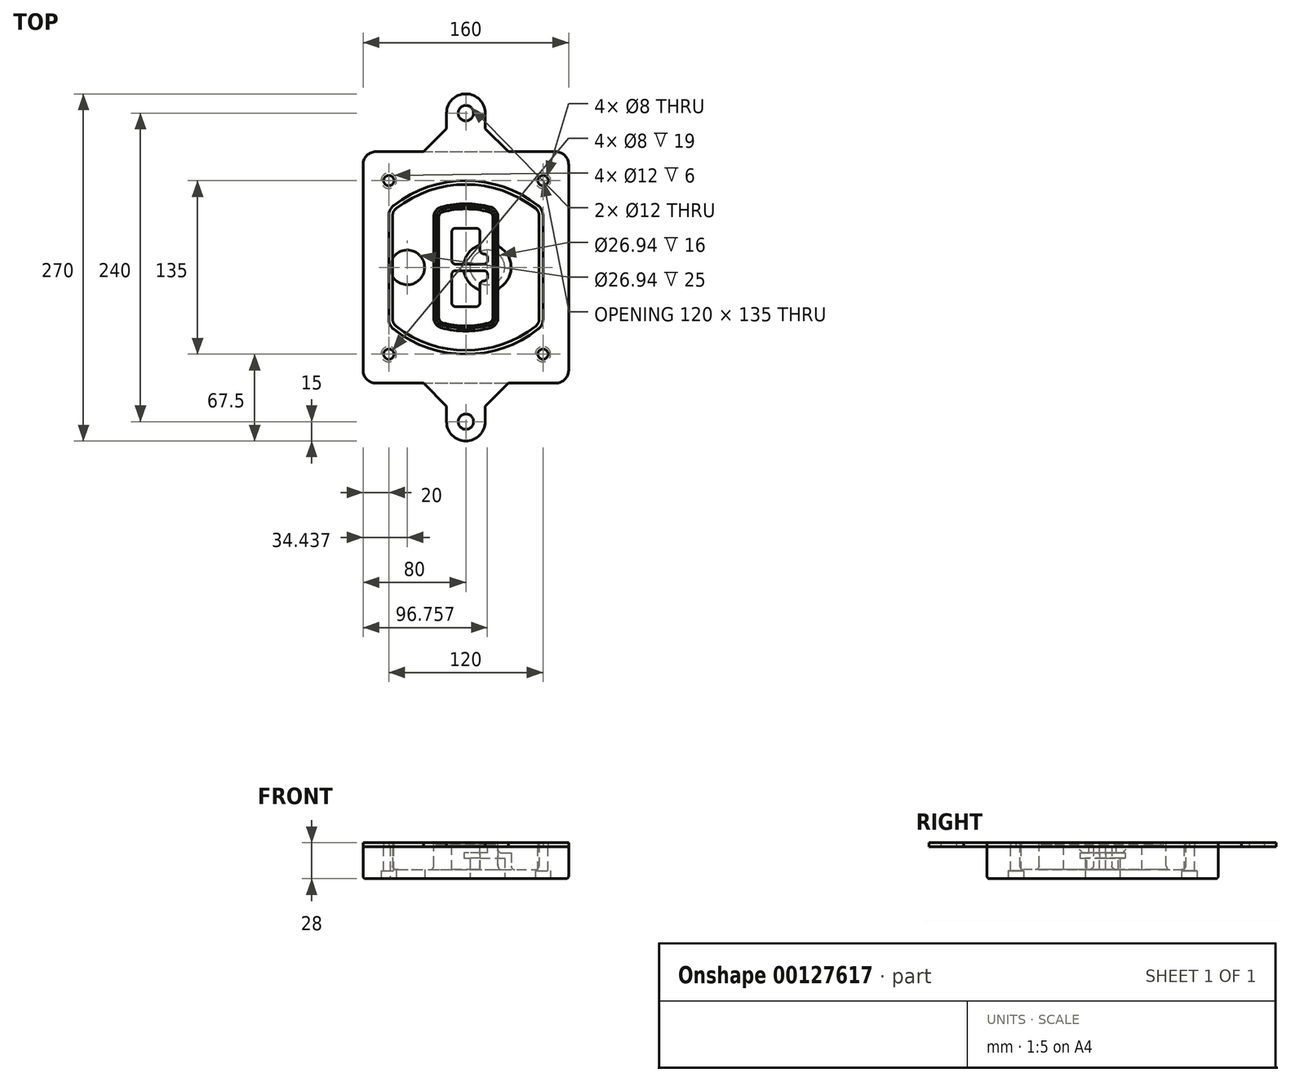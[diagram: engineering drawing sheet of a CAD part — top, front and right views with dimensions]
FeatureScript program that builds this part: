
annotation { "Feature Type Name" : "Feature", "Feature Type Description" : "" }
export const myFeature = defineFeature(function(context is Context, id is Id, definition is map)
    precondition{}
    {
        {
            var Q0;
            Q0=qCreatedBy(makeId("Top.planeOp"),FACE);
            var sketch = newSketch(context, id + "F0", { "sketchPlane" : qUnion([Q0])});
            skPoint(sketch, "E0.rect.middle", {"position": v(0, 0) * mm});
            skLineSegment(sketch, "E1.bottom", {"start": v(-70, -90) * mm, "end": v(70, -90) * mm});
            skLineSegment(sketch, "E1.top", {"start": v(-70, 90) * mm, "end": v(70, 90) * mm});
            skLineSegment(sketch, "E1.left", {"start": v(-80, -80) * mm, "end": v(-80, 80) * mm});
            skLineSegment(sketch, "E1.right", {"start": v(80, -80) * mm, "end": v(80, 80) * mm});
            skLineSegment(sketch, "E2", {"start": v(-80, 90) * mm, "end": v(80, -90) * mm, "construction": true});
            skLineSegment(sketch, "E3", {"start": v(80, 90) * mm, "end": v(-80, -90) * mm, "construction": true});
            skCircle(sketch, "E4", {"center": v(-60, 67.5) * mm, "radius": 4 * mm});
            skCircle(sketch, "E5", {"center": v(60, 67.5) * mm, "radius": 4 * mm});
            skCircle(sketch, "E6", {"center": v(60, -67.5) * mm, "radius": 4 * mm});
            skCircle(sketch, "E7", {"center": v(-60, -67.5) * mm, "radius": 4 * mm});
            skLineSegment(sketch, "E8", {"start": v(-60, 67.5) * mm, "end": v(60, 67.5) * mm, "construction": true});
            skLineSegment(sketch, "E9", {"start": v(60, 67.5) * mm, "end": v(60, -67.5) * mm, "construction": true});
            skLineSegment(sketch, "E10", {"start": v(60, -67.5) * mm, "end": v(-60, -67.5) * mm, "construction": true});
            skLineSegment(sketch, "E11", {"start": v(-60, -67.5) * mm, "end": v(-60, 67.5) * mm, "construction": true});
            skLineSegment(sketch, "E12", {"start": v(-60, 40.3) * mm, "end": v(-60, -40.3) * mm});
            skLineSegment(sketch, "E13", {"start": v(60, 40.3) * mm, "end": v(60, -40.3) * mm});
            skArc(sketch, "E14", {"start": v(56.15, 48.18) * mm, "mid": v(0, 67.5) * mm, "end": v(-56.15, 48.18) * mm});
            skArc(sketch, "E15", {"start": v(-56.15, -48.18) * mm, "mid": v(0, -67.5) * mm, "end": v(56.15, -48.18) * mm});
            skLineSegment(sketch, "E16", {"start": v(-60, 0) * mm, "end": v(60, 0) * mm, "construction": true});
            skPoint(sketch, "E17.visualSharp", {"position": v(-60, -45) * mm});
            skArc(sketch, "E17.filletArc", {"start": v(-60, -40.3) * mm, "mid": v(-58.99, -44.68) * mm, "end": v(-56.15, -48.18) * mm});
            skPoint(sketch, "E18.visualSharp", {"position": v(-60, 45) * mm});
            skArc(sketch, "E18.filletArc", {"start": v(-56.15, 48.18) * mm, "mid": v(-58.99, 44.68) * mm, "end": v(-60, 40.3) * mm});
            skPoint(sketch, "E19.visualSharp", {"position": v(60, 45) * mm});
            skArc(sketch, "E19.filletArc", {"start": v(60, 40.3) * mm, "mid": v(58.99, 44.68) * mm, "end": v(56.15, 48.18) * mm});
            skPoint(sketch, "E20.visualSharp", {"position": v(60, -45) * mm});
            skArc(sketch, "E20.filletArc", {"start": v(56.15, -48.18) * mm, "mid": v(58.99, -44.68) * mm, "end": v(60, -40.3) * mm});
            skPoint(sketch, "E21.visualSharp", {"position": v(-80, 90) * mm});
            skArc(sketch, "E21.filletArc", {"start": v(-70, 90) * mm, "mid": v(-77.07, 87.07) * mm, "end": v(-80, 80) * mm});
            skPoint(sketch, "E22.visualSharp", {"position": v(80, 90) * mm});
            skArc(sketch, "E22.filletArc", {"start": v(80, 80) * mm, "mid": v(77.07, 87.07) * mm, "end": v(70, 90) * mm});
            skPoint(sketch, "E23.visualSharp", {"position": v(80, -90) * mm});
            skArc(sketch, "E23.filletArc", {"start": v(70, -90) * mm, "mid": v(77.07, -87.07) * mm, "end": v(80, -80) * mm});
            skPoint(sketch, "E24.visualSharp", {"position": v(-80, -90) * mm});
            skArc(sketch, "E24.filletArc", {"start": v(-80, -80) * mm, "mid": v(-77.07, -87.07) * mm, "end": v(-70, -90) * mm});
            skArc(sketch, "E25.0", {"start": v(57, 40.3) * mm, "mid": v(56.3, 43.36) * mm, "end": v(54.3, 45.81) * mm});
            skLineSegment(sketch, "E25.1", {"start": v(57, 40.3) * mm, "end": v(57, -40.3) * mm});
            skArc(sketch, "E25.2", {"start": v(54.3, -45.81) * mm, "mid": v(56.3, -43.36) * mm, "end": v(57, -40.3) * mm});
            skArc(sketch, "E25.3", {"start": v(-54.3, -45.81) * mm, "mid": v(0, -64.5) * mm, "end": v(54.3, -45.81) * mm});
            skArc(sketch, "E25.4", {"start": v(-57, -40.3) * mm, "mid": v(-56.3, -43.36) * mm, "end": v(-54.3, -45.81) * mm});
            skArc(sketch, "E25.5", {"start": v(54.3, 45.81) * mm, "mid": v(0, 64.5) * mm, "end": v(-54.3, 45.81) * mm});
            skLineSegment(sketch, "E25.6", {"start": v(-57, 40.3) * mm, "end": v(-57, -40.3) * mm});
            skArc(sketch, "E25.7", {"start": v(-54.3, 45.81) * mm, "mid": v(-56.3, 43.36) * mm, "end": v(-57, 40.3) * mm});
            skArc(sketch, "E26.0", {"start": v(-58.62, 51.33) * mm, "mid": v(-62.58, 46.43) * mm, "end": v(-64, 40.3) * mm});
            skArc(sketch, "E26.1", {"start": v(58.62, 51.33) * mm, "mid": v(0, 71.5) * mm, "end": v(-58.62, 51.33) * mm});
            skArc(sketch, "E26.2", {"start": v(64, 40.3) * mm, "mid": v(62.58, 46.43) * mm, "end": v(58.62, 51.33) * mm});
            skLineSegment(sketch, "E26.3", {"start": v(64, 40.3) * mm, "end": v(64, -40.3) * mm});
            skArc(sketch, "E26.4", {"start": v(58.62, -51.33) * mm, "mid": v(62.58, -46.43) * mm, "end": v(64, -40.3) * mm});
            skLineSegment(sketch, "E26.5", {"start": v(-64, 40.3) * mm, "end": v(-64, -40.3) * mm});
            skArc(sketch, "E26.6", {"start": v(-58.62, -51.33) * mm, "mid": v(0, -71.5) * mm, "end": v(58.62, -51.33) * mm});
            skArc(sketch, "E26.7", {"start": v(-64, -40.3) * mm, "mid": v(-62.58, -46.43) * mm, "end": v(-58.62, -51.33) * mm});
            skSolve(sketch);
        }
        {
            var Q0;
            Q0=makeQuery(id+"F0.imprint","IMPRINT",FACE,{"disambiguationData":[TD([[makeQuery(id+"F0.imprint","IMPRINT",EDGE,{"derivedFrom":sQuery(id+"F0.wireOp",EDGE,"E1.bottom")}),1.0]])]});
            var Q1;
            Q1=makeQuery(id+"F0.imprint","IMPRINT",FACE,{"disambiguationData":[TD([[makeQuery(id+"F0.imprint","IMPRINT",EDGE,{"derivedFrom":sQuery(id+"F0.wireOp",EDGE,"E12")}),1.0]])]});
            var Q2;
            Q2=makeQuery(id+"F0.imprint","IMPRINT",FACE,{"disambiguationData":[TD([[makeQuery(id+"F0.imprint","IMPRINT",EDGE,{"derivedFrom":sQuery(id+"F0.wireOp",EDGE,"E25.0")}),1.0]])]});
            var Q3;
            Q3=makeQuery(id+"F0.imprint","IMPRINT",FACE,{"disambiguationData":[TD([[makeQuery(id+"F0.imprint","IMPRINT",EDGE,{"derivedFrom":sQuery(id+"F0.wireOp",EDGE,"E12")}),-1.0]])]});
            extrude(context, id + "F1", {"entities" : qUnion([Q0, Q1, Q2, Q3]), "oppositeDirection" : true, "depth" : 25 * mm});
        }
        {
            var Q0;
            Q0=makeQuery(id+"F0.imprint","IMPRINT",FACE,{"disambiguationData":[TD([[makeQuery(id+"F0.imprint","IMPRINT",EDGE,{"derivedFrom":sQuery(id+"F0.wireOp",EDGE,"E12")}),1.0]])]});
            extrude(context, id + "F2", {"entities" : qUnion([Q0]), "operationType" : NewBodyOperationType.ADD, "depth" : 3 * mm});
        }
        {
            var Q0;
            Q0=makeQuery(id+"F0.imprint","IMPRINT",FACE,{"disambiguationData":[TD([[makeQuery(id+"F0.imprint","IMPRINT",EDGE,{"derivedFrom":sQuery(id+"F0.wireOp",EDGE,"E25.0")}),1.0]])]});
            extrude(context, id + "F3", {"entities" : qUnion([Q0]), "operationType" : NewBodyOperationType.REMOVE, "oppositeDirection" : true, "depth" : 18 * mm});
        }
        {
            var Q0;
            Q0=makeQuery(id+"F2.opExtrude","CAP_FACE",FACE,{"disambiguationData":[OSD([sQuery(id+"F0.wireOp",EDGE,"E12"),sQuery(id+"F0.wireOp",EDGE,"E13"),sQuery(id+"F0.wireOp",EDGE,"E14"),sQuery(id+"F0.wireOp",EDGE,"E15"),sQuery(id+"F0.wireOp",EDGE,"E17.filletArc"),sQuery(id+"F0.wireOp",EDGE,"E18.filletArc"),sQuery(id+"F0.wireOp",EDGE,"E19.filletArc"),sQuery(id+"F0.wireOp",EDGE,"E20.filletArc"),sQuery(id+"F0.wireOp",EDGE,"E25.0"),sQuery(id+"F0.wireOp",EDGE,"E25.1"),sQuery(id+"F0.wireOp",EDGE,"E25.2"),sQuery(id+"F0.wireOp",EDGE,"E25.3"),sQuery(id+"F0.wireOp",EDGE,"E25.4"),sQuery(id+"F0.wireOp",EDGE,"E25.5"),sQuery(id+"F0.wireOp",EDGE,"E25.6"),sQuery(id+"F0.wireOp",EDGE,"E25.7")])],"isStart":false});
            var sketch = newSketch(context, id + "F4", { "sketchPlane" : qUnion([Q0])});
            skArc(sketch, "E27.0", {"start": v(-19.08, -46.97) * mm, "mid": v(0, -49.5) * mm, "end": v(19.08, -46.97) * mm});
            skArc(sketch, "E28.0", {"start": v(19.08, 46.97) * mm, "mid": v(0, 49.5) * mm, "end": v(-19.08, 46.97) * mm});
            skLineSegment(sketch, "E29", {"start": v(-25, 39.25) * mm, "end": v(-25, -39.25) * mm});
            skLineSegment(sketch, "E30", {"start": v(25, 39.25) * mm, "end": v(25, -39.25) * mm});
            skLineSegment(sketch, "E31", {"start": v(-25, 45.1) * mm, "end": v(25, 45.1) * mm, "construction": true});
            skLineSegment(sketch, "E32", {"start": v(-25, -45.1) * mm, "end": v(25, -45.1) * mm, "construction": true});
            skPoint(sketch, "E33.visualSharp", {"position": v(-25, 45.1) * mm});
            skArc(sketch, "E33.filletArc", {"start": v(-19.08, 46.97) * mm, "mid": v(-23.35, 44.11) * mm, "end": v(-25, 39.25) * mm});
            skPoint(sketch, "E34.visualSharp", {"position": v(25, 45.1) * mm});
            skArc(sketch, "E34.filletArc", {"start": v(25, 39.25) * mm, "mid": v(23.35, 44.11) * mm, "end": v(19.08, 46.97) * mm});
            skPoint(sketch, "E35.visualSharp", {"position": v(25, -45.1) * mm});
            skArc(sketch, "E35.filletArc", {"start": v(19.08, -46.97) * mm, "mid": v(23.35, -44.11) * mm, "end": v(25, -39.25) * mm});
            skPoint(sketch, "E36.visualSharp", {"position": v(-25, -45.1) * mm});
            skArc(sketch, "E36.filletArc", {"start": v(-25, -39.25) * mm, "mid": v(-23.35, -44.11) * mm, "end": v(-19.08, -46.97) * mm});
            skArc(sketch, "E37.0", {"start": v(54.3, 45.81) * mm, "mid": v(0, 64.5) * mm, "end": v(-54.3, 45.81) * mm});
            skArc(sketch, "E37.1", {"start": v(-54.3, 45.81) * mm, "mid": v(-56.3, 43.36) * mm, "end": v(-57, 40.3) * mm});
            skLineSegment(sketch, "E37.2", {"start": v(-57, 40.3) * mm, "end": v(-57, -40.3) * mm});
            skArc(sketch, "E37.3", {"start": v(-57, -40.3) * mm, "mid": v(-56.3, -43.36) * mm, "end": v(-54.3, -45.81) * mm});
            skArc(sketch, "E37.4", {"start": v(-54.3, -45.81) * mm, "mid": v(0, -64.5) * mm, "end": v(54.3, -45.81) * mm});
            skArc(sketch, "E37.5", {"start": v(54.3, -45.81) * mm, "mid": v(56.3, -43.36) * mm, "end": v(57, -40.3) * mm});
            skLineSegment(sketch, "E37.6", {"start": v(57, 40.3) * mm, "end": v(57, -40.3) * mm});
            skArc(sketch, "E37.7", {"start": v(57, 40.3) * mm, "mid": v(56.3, 43.36) * mm, "end": v(54.3, 45.81) * mm});
            skLineSegment(sketch, "E38.0", {"start": v(23, 39.25) * mm, "end": v(23, -39.25) * mm});
            skArc(sketch, "E38.1", {"start": v(18.56, -45.04) * mm, "mid": v(21.76, -42.9) * mm, "end": v(23, -39.25) * mm});
            skArc(sketch, "E38.2", {"start": v(-18.56, -45.04) * mm, "mid": v(0, -47.5) * mm, "end": v(18.56, -45.04) * mm});
            skArc(sketch, "E38.3", {"start": v(-23, -39.25) * mm, "mid": v(-21.76, -42.9) * mm, "end": v(-18.56, -45.04) * mm});
            skLineSegment(sketch, "E38.4", {"start": v(-23, 39.25) * mm, "end": v(-23, -39.25) * mm});
            skArc(sketch, "E38.5", {"start": v(23, 39.25) * mm, "mid": v(21.76, 42.9) * mm, "end": v(18.56, 45.04) * mm});
            skArc(sketch, "E38.6", {"start": v(-18.56, 45.04) * mm, "mid": v(-21.76, 42.9) * mm, "end": v(-23, 39.25) * mm});
            skArc(sketch, "E38.7", {"start": v(18.56, 45.04) * mm, "mid": v(0, 47.5) * mm, "end": v(-18.56, 45.04) * mm});
            skArc(sketch, "E39.0", {"start": v(21, 39.25) * mm, "mid": v(20.18, 41.68) * mm, "end": v(18.04, 43.1) * mm});
            skLineSegment(sketch, "E39.1", {"start": v(21, 39.25) * mm, "end": v(21, -39.25) * mm});
            skArc(sketch, "E39.2", {"start": v(18.04, -43.1) * mm, "mid": v(20.18, -41.68) * mm, "end": v(21, -39.25) * mm});
            skArc(sketch, "E39.3", {"start": v(-18.04, -43.1) * mm, "mid": v(0, -45.5) * mm, "end": v(18.04, -43.1) * mm});
            skArc(sketch, "E39.4", {"start": v(-21, -39.25) * mm, "mid": v(-20.18, -41.68) * mm, "end": v(-18.04, -43.1) * mm});
            skArc(sketch, "E39.5", {"start": v(18.04, 43.1) * mm, "mid": v(0, 45.5) * mm, "end": v(-18.04, 43.1) * mm});
            skLineSegment(sketch, "E39.6", {"start": v(-21, 39.25) * mm, "end": v(-21, -39.25) * mm});
            skArc(sketch, "E39.7", {"start": v(-18.04, 43.1) * mm, "mid": v(-20.18, 41.68) * mm, "end": v(-21, 39.25) * mm});
            skLineSegment(sketch, "E40", {"start": v(-25, 0) * mm, "end": v(25, 0) * mm, "construction": true});
            skLineSegment(sketch, "E41", {"start": v(-11, 5.5) * mm, "end": v(-11, 27.5) * mm});
            skLineSegment(sketch, "E42", {"start": v(-8, 30.5) * mm, "end": v(8, 30.5) * mm});
            skLineSegment(sketch, "E43", {"start": v(11, 27.5) * mm, "end": v(11, 13.5) * mm});
            skLineSegment(sketch, "E44", {"start": v(14, 10.5) * mm, "end": v(14, 10.5) * mm});
            skLineSegment(sketch, "E45", {"start": v(17, 7.5) * mm, "end": v(17, 5.5) * mm});
            skLineSegment(sketch, "E46", {"start": v(14, 2.5) * mm, "end": v(-8, 2.5) * mm});
            skPoint(sketch, "E47.visualSharp", {"position": v(-11, 30.5) * mm});
            skArc(sketch, "E47.filletArc", {"start": v(-8, 30.5) * mm, "mid": v(-10.12, 29.62) * mm, "end": v(-11, 27.5) * mm});
            skPoint(sketch, "E48.visualSharp", {"position": v(11, 30.5) * mm});
            skArc(sketch, "E48.filletArc", {"start": v(11, 27.5) * mm, "mid": v(10.12, 29.62) * mm, "end": v(8, 30.5) * mm});
            skPoint(sketch, "E49.visualSharp", {"position": v(11, 10.5) * mm});
            skArc(sketch, "E49.filletArc", {"start": v(11, 13.5) * mm, "mid": v(11.88, 11.38) * mm, "end": v(14, 10.5) * mm});
            skPoint(sketch, "E50.visualSharp", {"position": v(17, 10.5) * mm});
            skArc(sketch, "E50.filletArc", {"start": v(17, 7.5) * mm, "mid": v(16.12, 9.62) * mm, "end": v(14, 10.5) * mm});
            skPoint(sketch, "E51.visualSharp", {"position": v(17, 2.5) * mm});
            skArc(sketch, "E51.filletArc", {"start": v(14, 2.5) * mm, "mid": v(16.12, 3.38) * mm, "end": v(17, 5.5) * mm});
            skPoint(sketch, "E52.visualSharp", {"position": v(-11, 2.5) * mm});
            skArc(sketch, "E52.filletArc", {"start": v(-11, 5.5) * mm, "mid": v(-10.12, 3.38) * mm, "end": v(-8, 2.5) * mm});
            skLineSegment(sketch, "E53.0.MirrorCS", {"start": v(14, -2.5) * mm, "end": v(-8, -2.5) * mm});
            skArc(sketch, "E54.0.MirrorCS", {"start": v(-11, -5.5) * mm, "mid": v(-10.12, -3.38) * mm, "end": v(-8, -2.5) * mm});
            skLineSegment(sketch, "E55.0.MirrorCS", {"start": v(-11, -5.5) * mm, "end": v(-11, -27.5) * mm});
            skArc(sketch, "E56.0.MirrorCS", {"start": v(-8, -30.5) * mm, "mid": v(-10.12, -29.62) * mm, "end": v(-11, -27.5) * mm});
            skLineSegment(sketch, "E57.0.MirrorCS", {"start": v(-8, -30.5) * mm, "end": v(8, -30.5) * mm});
            skArc(sketch, "E58.0.MirrorCS", {"start": v(11, -27.5) * mm, "mid": v(10.12, -29.62) * mm, "end": v(8, -30.5) * mm});
            skLineSegment(sketch, "E59.0.MirrorCS", {"start": v(11, -27.5) * mm, "end": v(11, -13.5) * mm});
            skArc(sketch, "E60.0.MirrorCS", {"start": v(11, -13.5) * mm, "mid": v(11.88, -11.38) * mm, "end": v(14, -10.5) * mm});
            skArc(sketch, "E61.0.MirrorCS", {"start": v(17, -7.5) * mm, "mid": v(16.12, -9.62) * mm, "end": v(14, -10.5) * mm});
            skLineSegment(sketch, "E62.0.MirrorCS", {"start": v(17, -7.5) * mm, "end": v(17, -5.5) * mm});
            skArc(sketch, "E63.0.MirrorCS", {"start": v(14, -2.5) * mm, "mid": v(16.12, -3.38) * mm, "end": v(17, -5.5) * mm});
            skSolve(sketch);
        }
        {
            var Q0;
            Q0=makeQuery(id+"F4.imprint","IMPRINT",FACE,{"disambiguationData":[TD([[makeQuery(id+"F4.imprint","IMPRINT",EDGE,{"derivedFrom":sQuery(id+"F4.wireOp",EDGE,"E27.0")}),1.0]])]});
            var Q1;
            Q1=makeQuery(id+"F4.imprint","IMPRINT",FACE,{"disambiguationData":[TD([[makeQuery(id+"F4.imprint","IMPRINT",EDGE,{"derivedFrom":sQuery(id+"F4.wireOp",EDGE,"E38.0")}),-1.0]])]});
            var Q2;
            Q2=makeQuery(id+"F4.imprint","IMPRINT",FACE,{"disambiguationData":[TD([[makeQuery(id+"F4.imprint","IMPRINT",EDGE,{"derivedFrom":sQuery(id+"F4.wireOp",EDGE,"E39.0")}),1.0]])]});
            extrude(context, id + "F5", {"entities" : qUnion([Q0, Q1, Q2]), "operationType" : NewBodyOperationType.ADD, "endBound" : BoundingType.UP_TO_NEXT, "oppositeDirection" : true, "depth" : 25 * mm});
        }
        {
            var Q0;
            Q0=makeQuery(id+"F4.imprint","IMPRINT",FACE,{"disambiguationData":[TD([[makeQuery(id+"F4.imprint","IMPRINT",EDGE,{"derivedFrom":sQuery(id+"F4.wireOp",EDGE,"E38.0")}),-1.0]])]});
            extrude(context, id + "F6", {"entities" : qUnion([Q0]), "operationType" : NewBodyOperationType.REMOVE, "oppositeDirection" : true, "depth" : 2 * mm});
        }
        {
            var Q0;
            Q0=makeQuery(id+"F1.opExtrude","CAP_FACE",FACE,{"disambiguationData":[OSD([sQuery(id+"F0.wireOp",EDGE,"E1.bottom"),sQuery(id+"F0.wireOp",EDGE,"E1.top"),sQuery(id+"F0.wireOp",EDGE,"E1.left"),sQuery(id+"F0.wireOp",EDGE,"E1.right"),sQuery(id+"F0.wireOp",EDGE,"E4"),sQuery(id+"F0.wireOp",EDGE,"E5"),sQuery(id+"F0.wireOp",EDGE,"E6"),sQuery(id+"F0.wireOp",EDGE,"E7"),sQuery(id+"F0.wireOp",EDGE,"E21.filletArc"),sQuery(id+"F0.wireOp",EDGE,"E22.filletArc"),sQuery(id+"F0.wireOp",EDGE,"E23.filletArc"),sQuery(id+"F0.wireOp",EDGE,"E24.filletArc")])],"isStart":false});
            var sketch = newSketch(context, id + "F7", { "sketchPlane" : qUnion([Q0])});
            skCircle(sketch, "E64", {"center": v(16.76, 0) * mm, "radius": 13.47 * mm});
            skCircle(sketch, "E65", {"center": v(-45.56, 0) * mm, "radius": 13.47 * mm});
            skLineSegment(sketch, "E66", {"start": v(80, 0) * mm, "end": v(-80, 0) * mm});
            skCircle(sketch, "E67", {"center": v(16.76, 0) * mm, "radius": 18.47 * mm});
            skCircle(sketch, "E68", {"center": v(60, -67.5) * mm, "radius": 6 * mm});
            skCircle(sketch, "E69", {"center": v(-60, -67.5) * mm, "radius": 6 * mm});
            skCircle(sketch, "E70", {"center": v(-60, 67.5) * mm, "radius": 6 * mm});
            skCircle(sketch, "E71", {"center": v(60, 67.5) * mm, "radius": 6 * mm});
            skSolve(sketch);
        }
        {
            var Q0;
            {var subQ1=sQuery(id+"F7.wireOp",EDGE,"E66");var subQ4=sQuery(id+"F7.wireOp",EDGE,"E64");var subQ6=makeQuery(id+"F7.imprint","INTERSECT",VERTEX,{"disambiguationData":[OD(0.0)],"derivedFrom":[subQ4,subQ1]});Q0=makeQuery(id+"F7.imprint","IMPRINT",FACE,{"disambiguationData":[TD([[makeQuery(id+"F7.imprint","IMPRINT",EDGE,{"disambiguationData":[TD([[subQ6,-1.0]])],"derivedFrom":subQ4}),-1.0]])]});}
            var Q1;
            {var subQ0=sQuery(id+"F7.wireOp",EDGE,"E66");var subQ1=sQuery(id+"F7.wireOp",EDGE,"E64");var subQ3=makeQuery(id+"F7.imprint","INTERSECT",VERTEX,{"disambiguationData":[OD(0.0)],"derivedFrom":[subQ1,subQ0]});Q1=makeQuery(id+"F7.imprint","IMPRINT",FACE,{"disambiguationData":[TD([[makeQuery(id+"F7.imprint","IMPRINT",EDGE,{"disambiguationData":[TD([[subQ3,-1.0]])],"derivedFrom":subQ1}),1.0]])]});}
            var Q2;
            {var subQ0=sQuery(id+"F7.wireOp",EDGE,"E66");var subQ1=sQuery(id+"F7.wireOp",EDGE,"E64");var subQ3=makeQuery(id+"F7.imprint","INTERSECT",VERTEX,{"disambiguationData":[OD(0.0)],"derivedFrom":[subQ1,subQ0]});Q2=makeQuery(id+"F7.imprint","IMPRINT",FACE,{"disambiguationData":[TD([[makeQuery(id+"F7.imprint","IMPRINT",EDGE,{"disambiguationData":[TD([[subQ3,1.0]])],"derivedFrom":subQ1}),1.0]])]});}
            var Q3;
            {var subQ1=sQuery(id+"F7.wireOp",EDGE,"E66");var subQ4=sQuery(id+"F7.wireOp",EDGE,"E64");var subQ6=makeQuery(id+"F7.imprint","INTERSECT",VERTEX,{"disambiguationData":[OD(0.0)],"derivedFrom":[subQ4,subQ1]});Q3=makeQuery(id+"F7.imprint","IMPRINT",FACE,{"disambiguationData":[TD([[makeQuery(id+"F7.imprint","IMPRINT",EDGE,{"disambiguationData":[TD([[subQ6,1.0]])],"derivedFrom":subQ4}),-1.0]])]});}
            extrude(context, id + "F8", {"entities" : qUnion([Q0, Q1, Q2, Q3]), "operationType" : NewBodyOperationType.ADD, "oppositeDirection" : true, "depth" : 20 * mm});
        }
        {
            var Q0;
            {var subQ0=sQuery(id+"F7.wireOp",EDGE,"E66");var subQ1=sQuery(id+"F7.wireOp",EDGE,"E64");var subQ3=makeQuery(id+"F7.imprint","INTERSECT",VERTEX,{"disambiguationData":[OD(0.0)],"derivedFrom":[subQ1,subQ0]});Q0=makeQuery(id+"F7.imprint","IMPRINT",FACE,{"disambiguationData":[TD([[makeQuery(id+"F7.imprint","IMPRINT",EDGE,{"disambiguationData":[TD([[subQ3,-1.0]])],"derivedFrom":subQ1}),1.0]])]});}
            var Q1;
            {var subQ0=sQuery(id+"F7.wireOp",EDGE,"E66");var subQ1=sQuery(id+"F7.wireOp",EDGE,"E64");var subQ3=makeQuery(id+"F7.imprint","INTERSECT",VERTEX,{"disambiguationData":[OD(0.0)],"derivedFrom":[subQ1,subQ0]});Q1=makeQuery(id+"F7.imprint","IMPRINT",FACE,{"disambiguationData":[TD([[makeQuery(id+"F7.imprint","IMPRINT",EDGE,{"disambiguationData":[TD([[subQ3,1.0]])],"derivedFrom":subQ1}),1.0]])]});}
            extrude(context, id + "F9", {"entities" : qUnion([Q0, Q1]), "operationType" : NewBodyOperationType.REMOVE, "oppositeDirection" : true, "depth" : 16 * mm});
        }
        {
            var Q0;
            {var subQ0=sQuery(id+"F7.wireOp",EDGE,"E66");var subQ1=sQuery(id+"F7.wireOp",EDGE,"E65");var subQ3=makeQuery(id+"F7.imprint","INTERSECT",VERTEX,{"disambiguationData":[OD(0.0)],"derivedFrom":[subQ1,subQ0]});Q0=makeQuery(id+"F7.imprint","IMPRINT",FACE,{"disambiguationData":[TD([[makeQuery(id+"F7.imprint","IMPRINT",EDGE,{"disambiguationData":[TD([[subQ3,-1.0]])],"derivedFrom":subQ1}),1.0]])]});}
            var Q1;
            {var subQ0=sQuery(id+"F7.wireOp",EDGE,"E66");var subQ1=sQuery(id+"F7.wireOp",EDGE,"E65");var subQ3=makeQuery(id+"F7.imprint","INTERSECT",VERTEX,{"disambiguationData":[OD(0.0)],"derivedFrom":[subQ1,subQ0]});Q1=makeQuery(id+"F7.imprint","IMPRINT",FACE,{"disambiguationData":[TD([[makeQuery(id+"F7.imprint","IMPRINT",EDGE,{"disambiguationData":[TD([[subQ3,1.0]])],"derivedFrom":subQ1}),1.0]])]});}
            extrude(context, id + "F10", {"entities" : qUnion([Q0, Q1]), "operationType" : NewBodyOperationType.REMOVE, "oppositeDirection" : true, "depth" : 25 * mm});
        }
        {
            var Q0;
            Q0=makeQuery(id+"F7.imprint","IMPRINT",FACE,{"disambiguationData":[TD([[makeQuery(id+"F7.imprint","IMPRINT",EDGE,{"derivedFrom":sQuery(id+"F7.wireOp",EDGE,"E68")}),1.0]])]});
            var Q1;
            Q1=makeQuery(id+"F7.imprint","IMPRINT",FACE,{"disambiguationData":[TD([[makeQuery(id+"F7.imprint","IMPRINT",EDGE,{"derivedFrom":makeQuery(id+"F1.opExtrude","CAP_EDGE",EDGE,{"disambiguationData":[OSD([sQuery(id+"F0.wireOp",EDGE,"E5")])],"isStart":false})}),-1.0]])]});
            var Q2;
            Q2=makeQuery(id+"F7.imprint","IMPRINT",FACE,{"disambiguationData":[TD([[makeQuery(id+"F7.imprint","IMPRINT",EDGE,{"derivedFrom":sQuery(id+"F7.wireOp",EDGE,"E69")}),1.0]])]});
            var Q3;
            Q3=makeQuery(id+"F7.imprint","IMPRINT",FACE,{"disambiguationData":[TD([[makeQuery(id+"F7.imprint","IMPRINT",EDGE,{"derivedFrom":makeQuery(id+"F1.opExtrude","CAP_EDGE",EDGE,{"disambiguationData":[OSD([sQuery(id+"F0.wireOp",EDGE,"E4")])],"isStart":false})}),-1.0]])]});
            var Q4;
            Q4=makeQuery(id+"F7.imprint","IMPRINT",FACE,{"disambiguationData":[TD([[makeQuery(id+"F7.imprint","IMPRINT",EDGE,{"derivedFrom":sQuery(id+"F7.wireOp",EDGE,"E70")}),1.0]])]});
            var Q5;
            Q5=makeQuery(id+"F7.imprint","IMPRINT",FACE,{"disambiguationData":[TD([[makeQuery(id+"F7.imprint","IMPRINT",EDGE,{"derivedFrom":makeQuery(id+"F1.opExtrude","CAP_EDGE",EDGE,{"disambiguationData":[OSD([sQuery(id+"F0.wireOp",EDGE,"E7")])],"isStart":false})}),-1.0]])]});
            var Q6;
            Q6=makeQuery(id+"F7.imprint","IMPRINT",FACE,{"disambiguationData":[TD([[makeQuery(id+"F7.imprint","IMPRINT",EDGE,{"derivedFrom":sQuery(id+"F7.wireOp",EDGE,"E71")}),1.0]])]});
            var Q7;
            Q7=makeQuery(id+"F7.imprint","IMPRINT",FACE,{"disambiguationData":[TD([[makeQuery(id+"F7.imprint","IMPRINT",EDGE,{"derivedFrom":makeQuery(id+"F1.opExtrude","CAP_EDGE",EDGE,{"disambiguationData":[OSD([sQuery(id+"F0.wireOp",EDGE,"E6")])],"isStart":false})}),-1.0]])]});
            extrude(context, id + "F11", {"entities" : qUnion([Q0, Q1, Q2, Q3, Q4, Q5, Q6, Q7]), "operationType" : NewBodyOperationType.REMOVE, "oppositeDirection" : true, "depth" : 6 * mm});
        }
        {
            var Q0;
            Q0=makeQuery(id+"F9.boolean.opBoolean","COPY",FACE,{"derivedFrom":makeQuery(id+"F9.opExtrude","CAP_FACE",FACE,{"disambiguationData":[OSD([sQuery(id+"F7.wireOp",EDGE,"E64")])],"isStart":false})});
            var sketch = newSketch(context, id + "F12", { "sketchPlane" : qUnion([Q0])});
            skArc(sketch, "E72.0", {"start": v(11, 17.55) * mm, "mid": v(2.57, 11.82) * mm, "end": v(-1.54, 2.5) * mm});
            skArc(sketch, "E72.1", {"start": v(-1.54, -2.5) * mm, "mid": v(2.57, -11.82) * mm, "end": v(11, -17.55) * mm});
            skLineSegment(sketch, "E73", {"start": v(-1.54, -2.5) * mm, "end": v(14, -2.5) * mm});
            skLineSegment(sketch, "E74.0", {"start": v(14, 2.5) * mm, "end": v(-1.54, 2.5) * mm});
            skArc(sketch, "E74.1", {"start": v(14, 2.5) * mm, "mid": v(16.12, 3.38) * mm, "end": v(17, 5.5) * mm});
            skLineSegment(sketch, "E74.2", {"start": v(17, 7.5) * mm, "end": v(17, 5.5) * mm});
            skArc(sketch, "E74.3", {"start": v(17, 7.5) * mm, "mid": v(16.12, 9.62) * mm, "end": v(14, 10.5) * mm});
            skArc(sketch, "E74.4", {"start": v(11, 13.5) * mm, "mid": v(11.88, 11.38) * mm, "end": v(14, 10.5) * mm});
            skLineSegment(sketch, "E74.5", {"start": v(11, 17.55) * mm, "end": v(11, 13.5) * mm});
            skLineSegment(sketch, "E74.7", {"start": v(14, -2.5) * mm, "end": v(-1.54, -2.5) * mm});
            skArc(sketch, "E74.8", {"start": v(14, -2.5) * mm, "mid": v(16.12, -3.38) * mm, "end": v(17, -5.5) * mm});
            skLineSegment(sketch, "E74.9", {"start": v(17, -7.5) * mm, "end": v(17, -5.5) * mm});
            skArc(sketch, "E74.10", {"start": v(17, -7.5) * mm, "mid": v(16.12, -9.62) * mm, "end": v(14, -10.5) * mm});
            skArc(sketch, "E74.11", {"start": v(11, -13.5) * mm, "mid": v(11.88, -11.38) * mm, "end": v(14, -10.5) * mm});
            skLineSegment(sketch, "E74.12", {"start": v(11, -17.55) * mm, "end": v(11, -13.5) * mm});
            skPoint(sketch, "E75.orphan", {"position": v(11, -27.5) * mm});
            skPoint(sketch, "E76.orphan", {"position": v(-8, -2.5) * mm});
            skPoint(sketch, "E77.orphan", {"position": v(-8, 2.5) * mm});
            skPoint(sketch, "E78.orphan", {"position": v(11, 27.5) * mm});
            skSolve(sketch);
        }
        {
            var Q0;
            {var subQ7=sQuery(id+"F12.wireOp",EDGE,"E72.0");var subQ14=sQuery(id+"F12.wireOp",EDGE,"E72.1");var subQ16=sQuery(id+"F12.wireOp",EDGE,"E74.1");var subQ18=sQuery(id+"F12.wireOp",EDGE,"E74.8");Q0=qUnion([makeQuery(id+"F12.imprint","IMPRINT",FACE,{"disambiguationData":[TD([[makeQuery(id+"F12.imprint","IMPRINT",EDGE,{"derivedFrom":subQ7}),1.0]])]}),makeQuery(id+"F12.imprint","IMPRINT",FACE,{"disambiguationData":[TD([[makeQuery(id+"F12.imprint","IMPRINT",EDGE,{"derivedFrom":subQ14}),1.0]])]}),makeQuery(id+"F12.imprint","IMPRINT",FACE,{"disambiguationData":[TD([[makeQuery(id+"F12.imprint","IMPRINT",EDGE,{"derivedFrom":subQ16}),1.0]])]}),makeQuery(id+"F12.imprint","IMPRINT",FACE,{"disambiguationData":[TD([[makeQuery(id+"F12.imprint","IMPRINT",EDGE,{"derivedFrom":subQ18}),-1.0]])]})]);}
            var Q1;
            Q1=makeQuery(id+"F5.boolean.opBoolean","SPLIT",FACE,{"disambiguationData":[TD([makeQuery(id+"F5.opExtrude","SWEPT_FACE",FACE,{"disambiguationData":[OSD([sQuery(id+"F4.wireOp",EDGE,"E41")])]})])],"derivedFrom":makeQuery(id+"F3.boolean.opBoolean","COPY",FACE,{"derivedFrom":makeQuery(id+"F3.opExtrude","CAP_FACE",FACE,{"disambiguationData":[OSD([sQuery(id+"F0.wireOp",EDGE,"E25.0"),sQuery(id+"F0.wireOp",EDGE,"E25.1"),sQuery(id+"F0.wireOp",EDGE,"E25.2"),sQuery(id+"F0.wireOp",EDGE,"E25.3"),sQuery(id+"F0.wireOp",EDGE,"E25.4"),sQuery(id+"F0.wireOp",EDGE,"E25.5"),sQuery(id+"F0.wireOp",EDGE,"E25.6"),sQuery(id+"F0.wireOp",EDGE,"E25.7")])],"isStart":false})})});
            extrude(context, id + "F13", {"entities" : qUnion([Q0]), "operationType" : NewBodyOperationType.REMOVE, "endBound" : BoundingType.UP_TO_SURFACE, "endBoundEntityFace" : qUnion([Q1]), "depth" : 25 * mm});
        }
        {
            var Q0;
            Q0=makeQuery(id+"F3.boolean.opBoolean","COPY",EDGE,{"derivedFrom":makeQuery(id+"F3.opExtrude","CAP_EDGE",EDGE,{"disambiguationData":[OSD([sQuery(id+"F0.wireOp",EDGE,"E25.6")])],"isStart":false})});
            var Q1;
            Q1=makeQuery(id+"F8.boolean.opBoolean","INTERSECT",EDGE,{"derivedFrom":[makeQuery(id+"F5.opExtrude","SWEPT_FACE",FACE,{"disambiguationData":[OSD([sQuery(id+"F4.wireOp",EDGE,"E30")])]}),makeQuery(id+"F8.opExtrude","CAP_FACE",FACE,{"disambiguationData":[OSD([sQuery(id+"F7.wireOp",EDGE,"E67")])],"isStart":false})]});
            var Q2;
            Q2=makeQuery(id+"F8.boolean.opBoolean","INTERSECT",EDGE,{"disambiguationData":[OD(1.0)],"derivedFrom":[makeQuery(id+"F5.opExtrude","SWEPT_FACE",FACE,{"disambiguationData":[OSD([sQuery(id+"F4.wireOp",EDGE,"E30")])]}),makeQuery(id+"F8.opExtrude","SWEPT_FACE",FACE,{"disambiguationData":[OSD([sQuery(id+"F7.wireOp",EDGE,"E67")])]})]});
            var Q3;
            {var subQ0=sQuery(id+"F4.wireOp",EDGE,"E30");Q3=makeQuery(id+"F8.boolean.opBoolean","SPLIT",EDGE,{"disambiguationData":[TD([makeQuery(id+"F5.opExtrude","SWEPT_FACE",FACE,{"disambiguationData":[OSD([sQuery(id+"F4.wireOp",EDGE,"E35.filletArc")])]})])],"derivedFrom":makeQuery(id+"F5.opExtrude","CAP_EDGE",EDGE,{"disambiguationData":[OSD([subQ0])],"isStart":false})});}
            var Q4;
            {var subQ0=sQuery(id+"F0.wireOp",EDGE,"E25.7");var subQ1=sQuery(id+"F0.wireOp",EDGE,"E25.1");var subQ2=sQuery(id+"F0.wireOp",EDGE,"E25.6");var subQ3=sQuery(id+"F0.wireOp",EDGE,"E25.5");var subQ4=sQuery(id+"F0.wireOp",EDGE,"E25.4");var subQ5=sQuery(id+"F0.wireOp",EDGE,"E25.0");var subQ6=sQuery(id+"F0.wireOp",EDGE,"E25.2");var subQ7=sQuery(id+"F0.wireOp",EDGE,"E25.3");Q4=makeQuery(id+"F8.boolean.opBoolean","INTERSECT",EDGE,{"derivedFrom":[makeQuery(id+"F5.boolean.opBoolean","SPLIT",FACE,{"disambiguationData":[TD([makeQuery(id+"F2.opExtrude","SWEPT_FACE",FACE,{"disambiguationData":[OSD([subQ5])]})])],"derivedFrom":makeQuery(id+"F3.boolean.opBoolean","COPY",FACE,{"derivedFrom":makeQuery(id+"F3.opExtrude","CAP_FACE",FACE,{"disambiguationData":[OSD([subQ5,subQ1,subQ6,subQ7,subQ4,subQ3,subQ2,subQ0])],"isStart":false})})}),makeQuery(id+"F8.opExtrude","SWEPT_FACE",FACE,{"disambiguationData":[OSD([sQuery(id+"F7.wireOp",EDGE,"E67")])]})]});}
            var Q5;
            Q5=makeQuery(id+"F8.boolean.opBoolean","INTERSECT",EDGE,{"disambiguationData":[OD(0.0)],"derivedFrom":[makeQuery(id+"F5.opExtrude","SWEPT_FACE",FACE,{"disambiguationData":[OSD([sQuery(id+"F4.wireOp",EDGE,"E30")])]}),makeQuery(id+"F8.opExtrude","SWEPT_FACE",FACE,{"disambiguationData":[OSD([sQuery(id+"F7.wireOp",EDGE,"E67")])]})]});
            fillet(context, id + "F14", {"entities" : qUnion([Q0, Q1, Q2, Q3, Q4, Q5]), "radius" : 3 * mm, "tangentPropagation" : true, "allowEdgeOverflow" : false});
        }
        {
            var Q0;
            Q0=makeQuery(id+"F1.opExtrude","CAP_EDGE",EDGE,{"disambiguationData":[OSD([sQuery(id+"F0.wireOp",EDGE,"E1.bottom")])],"isStart":false});
            fillet(context, id + "F15", {"entities" : qUnion([Q0]), "radius" : 2 * mm, "tangentPropagation" : true, "allowEdgeOverflow" : false});
        }
        {
            var Q0;
            {var subQ0=sQuery(id+"F0.wireOp",EDGE,"E22.filletArc");var subQ1=sQuery(id+"F0.wireOp",EDGE,"E7");var subQ2=sQuery(id+"F0.wireOp",EDGE,"E6");var subQ3=sQuery(id+"F0.wireOp",EDGE,"E5");var subQ4=sQuery(id+"F0.wireOp",EDGE,"E4");var subQ5=sQuery(id+"F0.wireOp",EDGE,"E1.bottom");var subQ6=sQuery(id+"F0.wireOp",EDGE,"E21.filletArc");var subQ7=sQuery(id+"F0.wireOp",EDGE,"E1.top");var subQ8=sQuery(id+"F0.wireOp",EDGE,"E1.left");var subQ9=sQuery(id+"F0.wireOp",EDGE,"E1.right");var subQ10=sQuery(id+"F0.wireOp",EDGE,"E23.filletArc");var subQ11=sQuery(id+"F0.wireOp",EDGE,"E24.filletArc");Q0=makeQuery(id+"F2.boolean.opBoolean","SPLIT",FACE,{"disambiguationData":[TD([makeQuery(id+"F1.opExtrude","SWEPT_FACE",FACE,{"disambiguationData":[OSD([subQ5])]})])],"derivedFrom":makeQuery(id+"F1.opExtrude","CAP_FACE",FACE,{"disambiguationData":[OSD([subQ5,subQ7,subQ8,subQ9,subQ4,subQ3,subQ2,subQ1,subQ6,subQ0,subQ10,subQ11])],"isStart":true})});}
            var sketch = newSketch(context, id + "F16", { "sketchPlane" : qUnion([Q0])});
            skLineSegment(sketch, "E79", {"start": v(0, 90) * mm, "end": v(0, 120) * mm, "construction": true});
            skCircle(sketch, "E80", {"center": v(0, 120) * mm, "radius": 6 * mm});
            skArc(sketch, "E81", {"start": v(-15, 120) * mm, "mid": v(0, 135) * mm, "end": v(15, 120) * mm});
            skLineSegment(sketch, "E82", {"start": v(-33, 90) * mm, "end": v(-15, 108) * mm});
            skLineSegment(sketch, "E83", {"start": v(-15, 108) * mm, "end": v(-15, 120) * mm});
            skLineSegment(sketch, "E84", {"start": v(-33, 90) * mm, "end": v(33, 90) * mm});
            skLineSegment(sketch, "E85", {"start": v(33, 90) * mm, "end": v(15, 108) * mm});
            skLineSegment(sketch, "E86", {"start": v(15, 108) * mm, "end": v(15, 120) * mm});
            skLineSegment(sketch, "E87", {"start": v(-80, 0) * mm, "end": v(80, 0) * mm, "construction": true});
            skLineSegment(sketch, "E88.MirrorCS", {"start": v(33, 90) * mm, "end": v(-33, 90) * mm});
            skArc(sketch, "E89.MirrorCS", {"start": v(15, 120) * mm, "mid": v(0, 135) * mm, "end": v(-15, 120) * mm});
            skLineSegment(sketch, "E90.MirrorCS", {"start": v(80, 0) * mm, "end": v(-80, 0) * mm, "construction": true});
            skLineSegment(sketch, "E91.MirrorCS", {"start": v(33, -90) * mm, "end": v(15, -108) * mm});
            skLineSegment(sketch, "E92.MirrorCS", {"start": v(15, -108) * mm, "end": v(15, -120) * mm});
            skCircle(sketch, "E93.MirrorC", {"center": v(0, -120) * mm, "radius": 6 * mm});
            skArc(sketch, "E94.MirrorCS", {"start": v(-15, -120) * mm, "mid": v(0, -135) * mm, "end": v(15, -120) * mm});
            skLineSegment(sketch, "E95.MirrorCS", {"start": v(-15, -108) * mm, "end": v(-15, -120) * mm});
            skLineSegment(sketch, "E96.MirrorCS", {"start": v(-33, -90) * mm, "end": v(-15, -108) * mm});
            skLineSegment(sketch, "E97.MirrorCS", {"start": v(33, -90) * mm, "end": v(-33, -90) * mm});
            skLineSegment(sketch, "E98.MirrorCS", {"start": v(0, -90) * mm, "end": v(0, -120) * mm, "construction": true});
            skSolve(sketch);
        }
        {
            var Q0;
            Q0 = qSketchRegion(id + "F16", true);
            var Q1;
            {var subQ4=sQuery(id+"F16.wireOp",EDGE,"E84");Q1=makeQuery(id+"F16.imprint","IMPRINT",FACE,{"disambiguationData":[TD([[makeQuery(id+"F16.imprint","IMPRINT",EDGE,{"derivedFrom":subQ4}),-1.0]])]});}
            var Q2;
            Q2=makeQuery(id+"F2.opExtrude","CAP_FACE",FACE,{"disambiguationData":[OSD([sQuery(id+"F0.wireOp",EDGE,"E12"),sQuery(id+"F0.wireOp",EDGE,"E13"),sQuery(id+"F0.wireOp",EDGE,"E14"),sQuery(id+"F0.wireOp",EDGE,"E15"),sQuery(id+"F0.wireOp",EDGE,"E17.filletArc"),sQuery(id+"F0.wireOp",EDGE,"E18.filletArc"),sQuery(id+"F0.wireOp",EDGE,"E19.filletArc"),sQuery(id+"F0.wireOp",EDGE,"E20.filletArc"),sQuery(id+"F0.wireOp",EDGE,"E25.0"),sQuery(id+"F0.wireOp",EDGE,"E25.1"),sQuery(id+"F0.wireOp",EDGE,"E25.2"),sQuery(id+"F0.wireOp",EDGE,"E25.3"),sQuery(id+"F0.wireOp",EDGE,"E25.4"),sQuery(id+"F0.wireOp",EDGE,"E25.5"),sQuery(id+"F0.wireOp",EDGE,"E25.6"),sQuery(id+"F0.wireOp",EDGE,"E25.7")])],"isStart":false});
            extrude(context, id + "F17", {"entities" : qUnion([Q0, Q1]), "endBound" : BoundingType.UP_TO_SURFACE, "endBoundEntityFace" : qUnion([Q2]), "depth" : 25 * mm});
        }
    });
